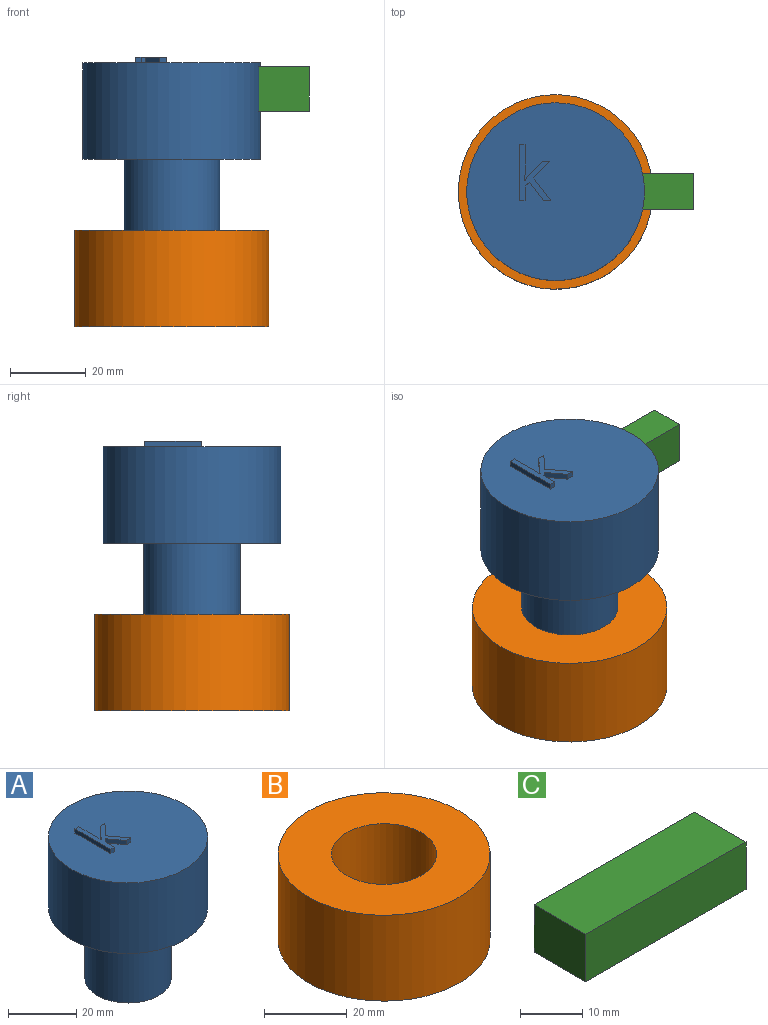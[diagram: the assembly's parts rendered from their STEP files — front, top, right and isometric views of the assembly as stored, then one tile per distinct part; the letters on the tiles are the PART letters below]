
ASSEMBLY  parts=3 mates=2
PART A: 21 faces, bbox 46.8x46.8x52.3 mm
  f0: plane 46.84x46.84mm, normal (0,0,1), area 1678.8mm2, adj f3,f5,f6,f7,f8,f9,f10,f11
  f1: cylinder r=12.7mm len=25.4mm, axis (0,0,-1), area 2026.8mm2, adj f2,f4
  f2: plane 25.4x25.4mm, normal (0,0,-1), area 506.7mm2, adj f1
  f3: cylinder r=23.42mm len=46.84mm, axis (0,0,-1), area 3737.7mm2, adj f0,f4
  f4: plane 46.84x46.84mm, normal (0,0,-1), area 1216.5mm2, adj f1,f3
  f5: plane 1.52x0.08mm, normal (0,1,0), area 0.1mm2, adj f0,f6,f19,f20
  f6: extruded ~1.63x1.52mm, area 2.5mm2, adj f0,f5,f7,f20
  f7: plane 7.9x1.52mm, normal (1,0,0), area 12mm2, adj f0,f6,f8,f20
  f8: plane 1.57x1.52mm, normal (0,1,0), area 2.4mm2, adj f0,f7,f9,f20
  f9: plane 14.89x1.52mm, normal (-1,0,0), area 22.7mm2, adj f0,f8,f10,f20
  f10: plane 1.57x1.52mm, normal (0,-1,0), area 2.4mm2, adj f0,f9,f11,f20
  f11: plane 3.92x1.52mm, normal (1,0,0), area 6mm2, adj f0,f10,f12,f20
  f12: plane 1.52x1.19mm, normal (0.65,-0.76,0), area 2.4mm2, adj f0,f11,f13,f20
  f13: plane 4.96x3.71mm, normal (-0.8,-0.6,0), area 9.4mm2, adj f0,f12,f14,f20
  f14: plane 1.92x1.52mm, normal (0,-1,0), area 2.9mm2, adj f0,f13,f15,f20
  f15: plane 6.02x4.55mm, normal (0.8,0.6,0), area 11.5mm2, adj f0,f14,f16,f20
  f16: plane 4.47x4.25mm, normal (0.72,-0.69,0), area 9.4mm2, adj f0,f15,f17,f20
  f17: plane 1.89x1.52mm, normal (0,1,0), area 2.9mm2, adj f0,f16,f18,f20
  f18: plane 3.59x3.39mm, normal (-0.73,0.69,0), area 7.5mm2, adj f0,f17,f19,f20
  f19: extruded ~1.53x1.52mm, area 3mm2, adj f0,f5,f18,f20
  f20: plane 14.89x8.39mm, normal (0,0,1), area 44.4mm2, adj f5,f6,f7,f8,f9,f10,f11,f12
PART B: 4 faces, bbox 51.3x51.3x25.4 mm
  f0: cylinder r=12.7mm len=25.4mm, axis (0,0,-1), area 2026.8mm2, adj f2,f3
  f1: cylinder r=25.63mm len=51.26mm, axis (0,0,-1), area 4090.1mm2, adj f2,f3
  f2: plane 51.26x51.26mm, normal (0,0,1), area 1556.7mm2, adj f0,f1
  f3: plane 51.26x51.26mm, normal (0,0,-1), area 1556.7mm2, adj f0,f1
PART C: 6 faces, bbox 36.3x11.7x9.3 mm
  f0: plane 36.32x11.73mm, normal (0,0,-1), area 425.9mm2, adj f1,f3,f4,f5
  f1: plane 36.32x9.31mm, normal (0,1,0), area 338.1mm2, adj f0,f2,f4,f5
  f2: plane 36.32x11.73mm, normal (0,0,1), area 425.9mm2, adj f1,f3,f4,f5
  f3: plane 36.32x9.31mm, normal (0,-1,0), area 338.1mm2, adj f0,f2,f4,f5
  f4: plane 11.73x9.31mm, normal (1,0,0), area 109.1mm2, adj f0,f1,f2,f3
  f5: plane 11.73x9.31mm, normal (-1,0,0), area 109.1mm2, adj f0,f1,f2,f3
PLACE A rot(axis=(0,0,1),0deg) t=(-53.14,-56.49,-1.6)mm
PLACE B t=(-36.77,54.75,-20.33)mm fixed
PLACE C rot(axis=(-1,0,0),90deg) t=(-49.85,-62.81,74.57)mm
MATE fastened C.f1 <-> A.f1  axis (0,0,-1) through (-3.88,-7.33,36.5)mm
MATE slider B.f0 <-> A.f1  axis (0,0,-1) through (-3.88,-7.33,-20.33)mm
